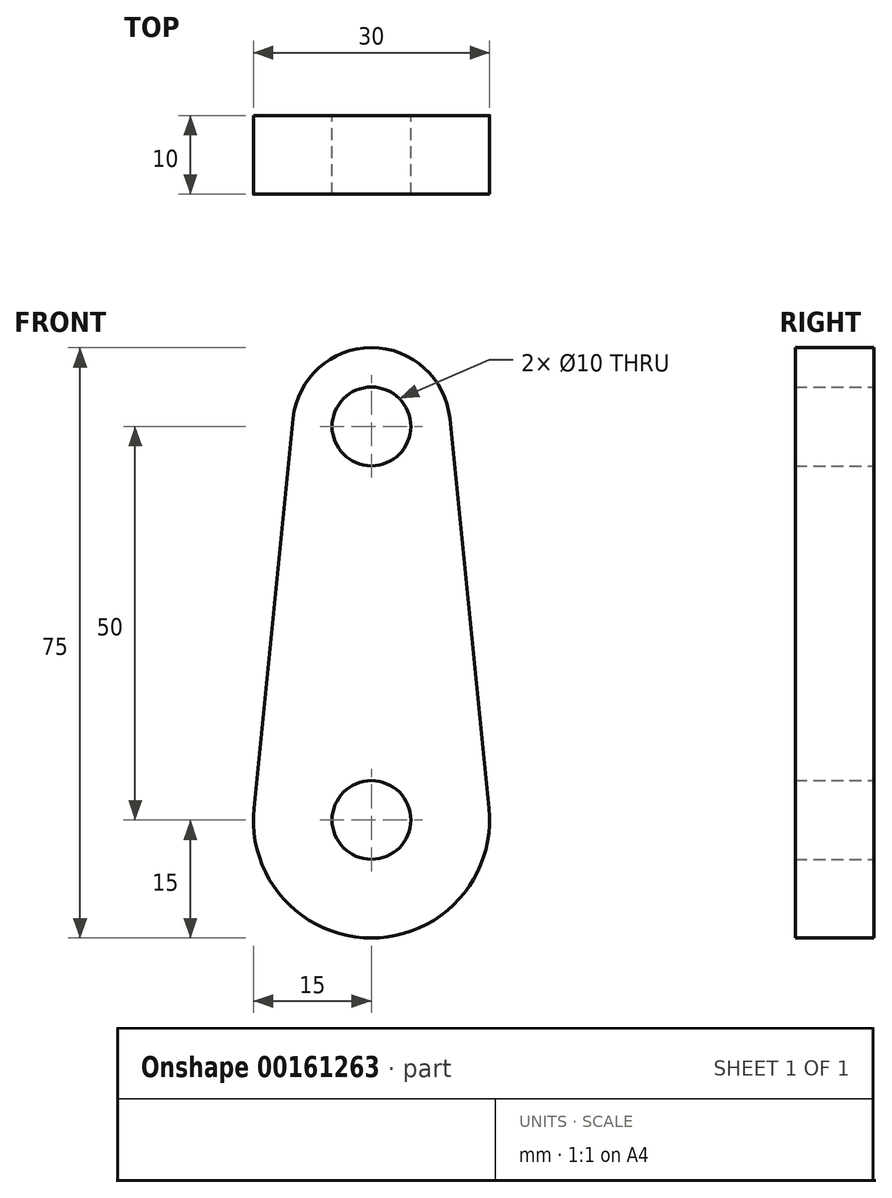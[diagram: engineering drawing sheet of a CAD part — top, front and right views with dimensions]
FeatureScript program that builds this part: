
annotation { "Feature Type Name" : "Feature", "Feature Type Description" : "" }
export const myFeature = defineFeature(function(context is Context, id is Id, definition is map)
    precondition{}
    {
        {
            var Q0;
            Q0=qCreatedBy(makeId("Front.planeOp"),FACE);
            var sketch = newSketch(context, id + "F0", { "sketchPlane" : qUnion([Q0])});
            skCircle(sketch, "E0", {"center": v(0, 0) * mm, "radius": 15 * mm});
            skCircle(sketch, "E1", {"center": v(0, 50) * mm, "radius": 10 * mm});
            skLineSegment(sketch, "E2", {"start": v(-14.92, 1.5) * mm, "end": v(-9.95, 51) * mm});
            skLineSegment(sketch, "E3", {"start": v(9.95, 51) * mm, "end": v(14.92, 1.5) * mm});
            skCircle(sketch, "E4.0", {"center": v(0, 50) * mm, "radius": 5 * mm});
            skCircle(sketch, "E5.0", {"center": v(0, 0) * mm, "radius": 5 * mm});
            skSolve(sketch);
        }
        {
            var Q0;
            Q0=makeQuery(id+"F0.imprint","IMPRINT",FACE,{"disambiguationData":[TD([[makeQuery(id+"F0.imprint","IMPRINT",EDGE,{"derivedFrom":sQuery(id+"F0.wireOp",EDGE,"E4.0")}),-1.0]])]});
            var Q1;
            {var subQ0=sQuery(id+"F0.wireOp",EDGE,"E2");Q1=makeQuery(id+"F0.imprint","IMPRINT",FACE,{"disambiguationData":[TD([[makeQuery(id+"F0.imprint","IMPRINT",EDGE,{"derivedFrom":subQ0}),-1.0]])]});}
            var Q2;
            Q2=makeQuery(id+"F0.imprint","IMPRINT",FACE,{"disambiguationData":[TD([[makeQuery(id+"F0.imprint","IMPRINT",EDGE,{"derivedFrom":sQuery(id+"F0.wireOp",EDGE,"E5.0")}),-1.0]])]});
            extrude(context, id + "F1", {"entities" : qUnion([Q0, Q1, Q2]), "depth" : 10 * mm, "symmetric" : true});
        }
    });
